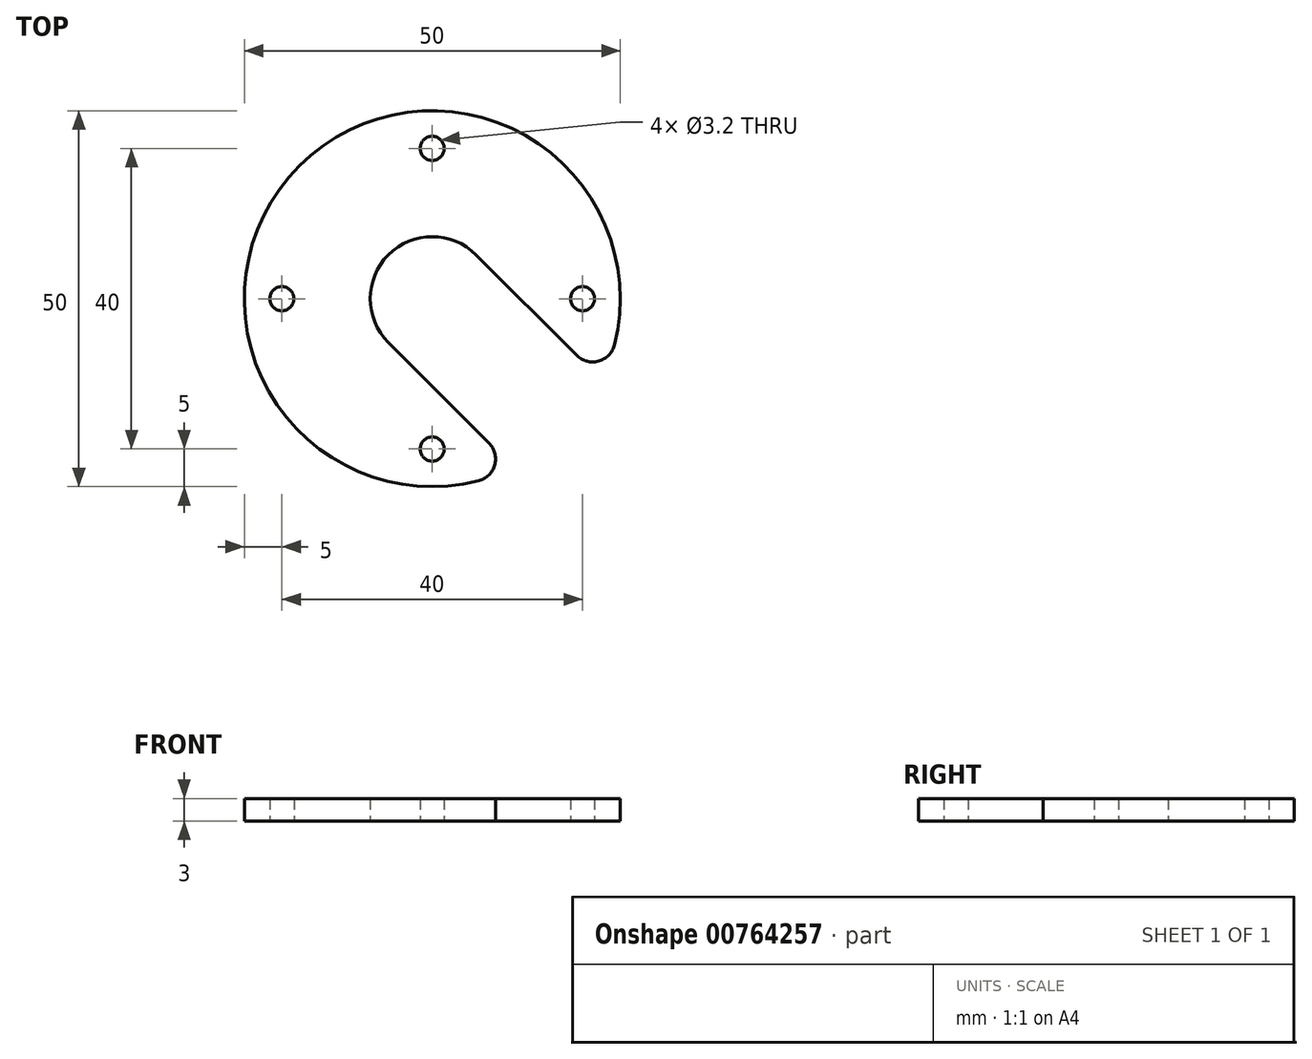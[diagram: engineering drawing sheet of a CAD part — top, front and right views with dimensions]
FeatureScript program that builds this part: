
annotation { "Feature Type Name" : "Feature", "Feature Type Description" : "" }
export const myFeature = defineFeature(function(context is Context, id is Id, definition is map)
    precondition{}
    {
        {
            var Q0;
            Q0=qCreatedBy(makeId("Top.planeOp"),FACE);
            var sketch = newSketch(context, id + "F0", { "sketchPlane" : qUnion([Q0])});
            skArc(sketch, "E0", {"start": v(24.23, -6.15) * mm, "mid": v(-17.68, 17.68) * mm, "end": v(6.15, -24.23) * mm});
            skCircle(sketch, "E1", {"center": v(0, 20) * mm, "radius": 1.6 * mm});
            skCircle(sketch, "E2", {"center": v(20, 0) * mm, "radius": 1.6 * mm});
            skCircle(sketch, "E3", {"center": v(0, -20) * mm, "radius": 1.6 * mm});
            skCircle(sketch, "E4", {"center": v(-20, 0) * mm, "radius": 1.6 * mm});
            skCircle(sketch, "E5", {"center": v(0, 0) * mm, "radius": 8.25 * mm});
            skLineSegment(sketch, "E6", {"start": v(-5.83, -5.83) * mm, "end": v(7.53, -19.2) * mm});
            skLineSegment(sketch, "E7", {"start": v(0, 0) * mm, "end": v(-5.83, -5.83) * mm});
            skLineSegment(sketch, "E8", {"start": v(5.83, 5.83) * mm, "end": v(19.2, -7.53) * mm});
            skPoint(sketch, "E9.visualSharp", {"position": v(10.85, -22.52) * mm});
            skArc(sketch, "E9.filletArc", {"start": v(6.15, -24.23) * mm, "mid": v(8.3, -22.12) * mm, "end": v(7.53, -19.2) * mm});
            skPoint(sketch, "E10.visualSharp", {"position": v(22.52, -10.85) * mm});
            skArc(sketch, "E10.filletArc", {"start": v(19.2, -7.53) * mm, "mid": v(22.12, -8.3) * mm, "end": v(24.23, -6.15) * mm});
            skSolve(sketch);
        }
        {
            var Q0;
            Q0=makeQuery(id+"F0.imprint","IMPRINT",FACE,{"disambiguationData":[TD([[makeQuery(id+"F0.imprint","IMPRINT",EDGE,{"derivedFrom":sQuery(id+"F0.wireOp",EDGE,"E0")}),1.0]])]});
            extrude(context, id + "F1", {"entities" : qUnion([Q0]), "depth" : 3 * mm, "offsetDistance" : 25 * mm});
        }
    });
